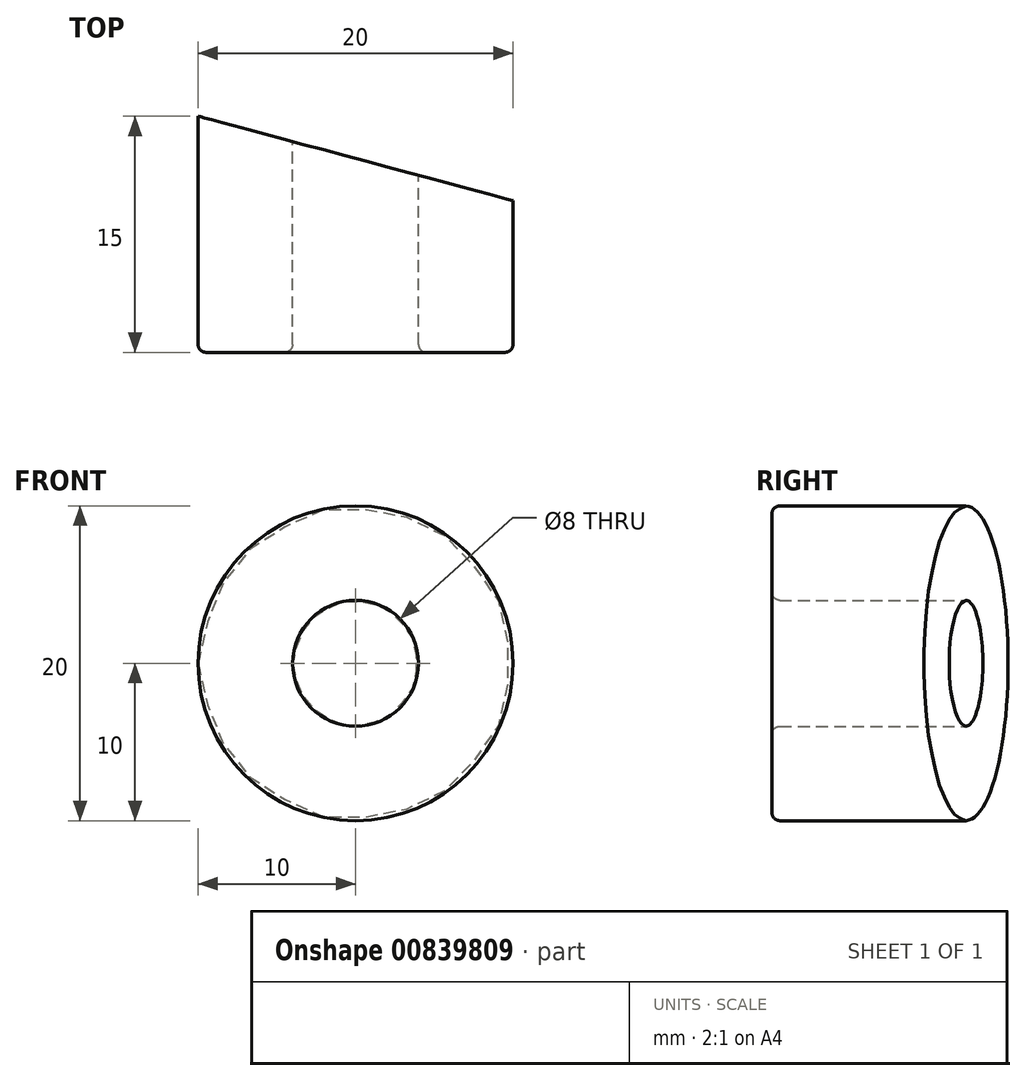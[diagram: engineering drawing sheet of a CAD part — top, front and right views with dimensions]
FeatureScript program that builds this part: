
annotation { "Feature Type Name" : "Feature", "Feature Type Description" : "" }
export const myFeature = defineFeature(function(context is Context, id is Id, definition is map)
    precondition{}
    {
        {
            var Q0;
            Q0=qCreatedBy(makeId("Front.planeOp"),FACE);
            var sketch = newSketch(context, id + "F0", { "sketchPlane" : qUnion([Q0])});
            skCircle(sketch, "E0", {"center": v(0, 0) * mm, "radius": 10 * mm});
            skCircle(sketch, "E1", {"center": v(0, 0) * mm, "radius": 4 * mm});
            skSolve(sketch);
        }
        {
            var Q0;
            Q0 = qSketchRegion(id + "F0", true);
            extrude(context, id + "F1", {"entities" : qUnion([Q0]), "depth" : 15 * mm, "offsetDistance" : 25 * mm});
        }
        {
            var Q0;
            Q0=makeQuery(id+"F1.opExtrude","CAP_EDGE",EDGE,{"disambiguationData":[OSD([sQuery(id+"F0.wireOp",EDGE,"E0")])],"isStart":false});
            var Q1;
            Q1=makeQuery(id+"F1.opExtrude","CAP_EDGE",EDGE,{"disambiguationData":[OSD([sQuery(id+"F0.wireOp",EDGE,"E1")])],"isStart":false});
            fillet(context, id + "F2", {"entities" : qUnion([Q0, Q1]), "radius" : 0.5 * mm, "tangentPropagation" : true, "allowEdgeOverflow" : false});
        }
        {
            var Q0;
            Q0=qCreatedBy(makeId("Top.planeOp"),FACE);
            var sketch = newSketch(context, id + "F3", { "sketchPlane" : qUnion([Q0])});
            skLineSegment(sketch, "E2", {"start": v(-10, 0) * mm, "end": v(10, 0) * mm});
            skLineSegment(sketch, "E3", {"start": v(10, 0) * mm, "end": v(10, -5.36) * mm});
            skLineSegment(sketch, "E4", {"start": v(10, -5.36) * mm, "end": v(-10, 0) * mm});
            skSolve(sketch);
        }
        {
            var Q0;
            Q0 = qSketchRegion(id + "F3", true);
            extrude(context, id + "F4", {"entities" : qUnion([Q0]), "operationType" : NewBodyOperationType.REMOVE, "depth" : 10 * mm, "offsetDistance" : 25 * mm, "hasSecondDirection" : true, "secondDirectionOppositeDirection" : true, "secondDirectionDepth" : 10 * mm});
        }
    });
